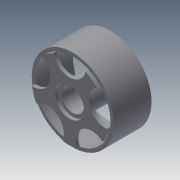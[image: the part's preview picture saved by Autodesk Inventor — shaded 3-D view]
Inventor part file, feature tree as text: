
AUTODESK INVENTOR PART (.ipt)
format: ipt  version: 2015 (Build 190159000, 159)  size: 141,824 bytes
history: native  units: in
note: dims shown in document units (in); Inventor stores cm internally (conversion verified against a paired STEP export)
features: projected_geometry x4, extrude x3, sketch x3, pattern_circular x1
ambient origin geometry x8: Origin, YZ Plane, XZ Plane, XY Plane, X Axis, Y Axis, Z Axis, Center Point
bodies: Solid1 (feature_tree)
feature tree (11):
  extrude  "Extrusion1"  Depth=0.05in
  extrude  "Extrusion2"  Depth=0.05in
  extrude  "Extrusion3"  Depth=0.05in TaperAngle=0.0deg
  pattern_circular  "Circular Pattern1"  [2 undecoded]
  sketch  "Sketch1"  dims[d0=0.05in d1=0.35in]
  sketch  "Sketch2"  dims[d2=0.05in d3=0.44in]
  projected_geometry  "Projected Loop1"
  projected_geometry  "Projected Loop2"
  sketch  "Sketch3"  dims[d4=0.57in d5=0.0in d6=0.05in d7=0.0in d9=0.5in d10=0.05in d11=0.0in d12=1.9685in d13=360.0deg]
  projected_geometry  "Projected Loop3"
  projected_geometry  "Projected Loop4"
note: 2 required parameter values undecoded (feature->parameter linkage not recoverable at this tier; creation-order binding heuristic only, values carry confidence <= 0.55)
